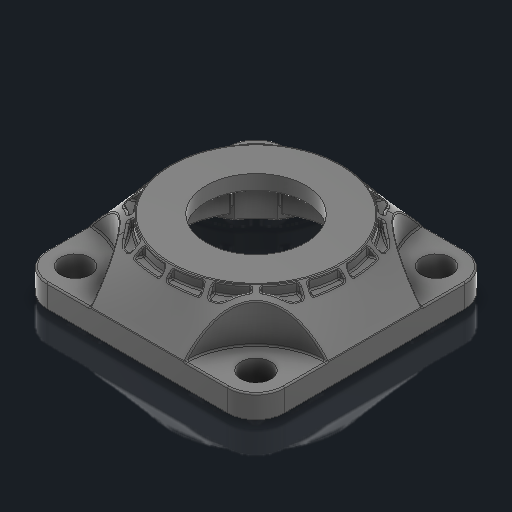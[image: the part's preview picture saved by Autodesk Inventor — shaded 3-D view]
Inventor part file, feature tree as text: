
AUTODESK INVENTOR PART (.ipt)
format: ipt  version: 2023.2 (Build 272271030, 271C)  size: 3,407,360 bytes
history: native  units: in
note: dims shown in document units (in); Inventor stores cm internally (conversion verified against a paired STEP export)
features: fillet x1
ambient origin geometry x8: Origin, YZ Plane, XZ Plane, XY Plane, X Axis, Y Axis, Z Axis, Center Point
bodies: Solid1 (feature_tree)
feature tree (1):
  fillet  "Fillet52"  [1 undecoded]
note: 1 required parameter value undecoded (feature->parameter linkage not recoverable at this tier; creation-order binding heuristic only, values carry confidence <= 0.55)
